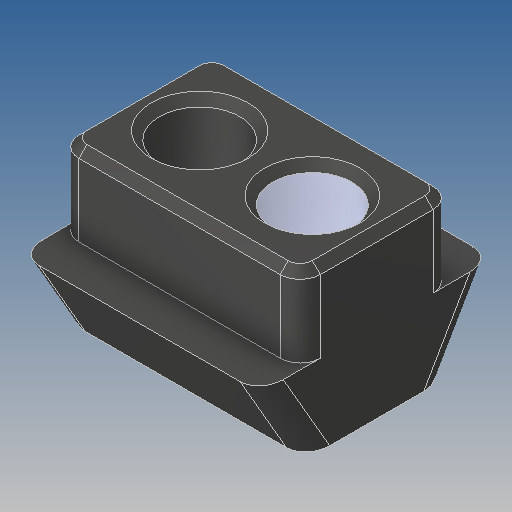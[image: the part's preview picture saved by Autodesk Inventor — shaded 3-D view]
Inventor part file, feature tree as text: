
AUTODESK INVENTOR PART (.ipt)
format: ipt  version: 2019 (Build 230136000, 136)  size: 143,360 bytes
history: native  units: mm
features: chamfer x1
ambient origin geometry x8: Origin, YZ Plane, XZ Plane, XY Plane, X Axis, Y Axis, Z Axis, Center Point
bodies: Solid1 (feature_tree)
feature tree (1):
  chamfer  "Chamfer1 - .010x45deg"  [1 undecoded]
note: 1 required parameter value undecoded (feature->parameter linkage not recoverable at this tier; creation-order binding heuristic only, values carry confidence <= 0.55)
